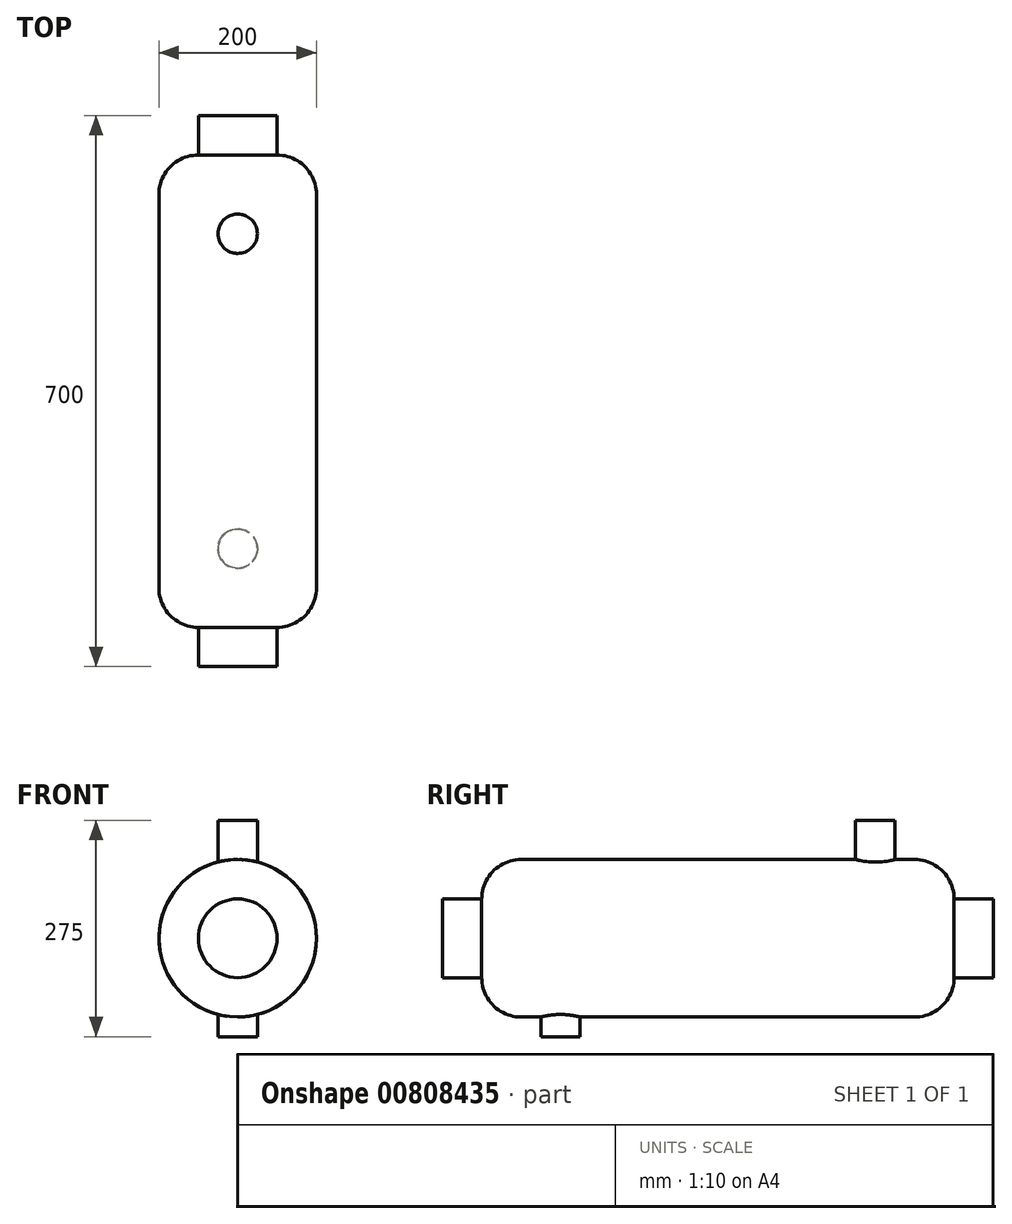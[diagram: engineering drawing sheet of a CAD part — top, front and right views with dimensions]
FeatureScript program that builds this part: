
annotation { "Feature Type Name" : "Feature", "Feature Type Description" : "" }
export const myFeature = defineFeature(function(context is Context, id is Id, definition is map)
    precondition{}
    {
        {
            var Q0;
            Q0=qCreatedBy(makeId("Right.planeOp"),FACE);
            var sketch = newSketch(context, id + "F0", { "sketchPlane" : qUnion([Q0])});
            skPoint(sketch, "E0.middle", {"position": v(0, 0) * mm});
            skLineSegment(sketch, "E1", {"start": v(0, 0) * mm, "end": v(-300, 0) * mm});
            skLineSegment(sketch, "E2", {"start": v(-300, 0) * mm, "end": v(-300, 50) * mm});
            skLineSegment(sketch, "E3", {"start": v(-250, 100) * mm, "end": v(250, 100) * mm});
            skLineSegment(sketch, "E4", {"start": v(300, 50) * mm, "end": v(300, 0) * mm});
            skLineSegment(sketch, "E5", {"start": v(300, 0) * mm, "end": v(0, 0) * mm});
            skPoint(sketch, "E6.visualSharp", {"position": v(-300, 100) * mm});
            skArc(sketch, "E6.filletArc", {"start": v(-250, 100) * mm, "mid": v(-285.36, 85.36) * mm, "end": v(-300, 50) * mm});
            skPoint(sketch, "E7.visualSharp", {"position": v(300, 100) * mm});
            skArc(sketch, "E7.filletArc", {"start": v(300, 50) * mm, "mid": v(285.36, 85.36) * mm, "end": v(250, 100) * mm});
            skLineSegment(sketch, "E8.bottom", {"start": v(-300, 0) * mm, "end": v(-300, 0) * mm});
            skLineSegment(sketch, "E8.top", {"start": v(-300, 50) * mm, "end": v(-300, 50) * mm});
            skLineSegment(sketch, "E9.bottom", {"start": v(-300, 0) * mm, "end": v(-350, 0) * mm});
            skLineSegment(sketch, "E9.top", {"start": v(-300, 50) * mm, "end": v(-350, 50) * mm});
            skLineSegment(sketch, "E9.right", {"start": v(-350, 0) * mm, "end": v(-350, 50) * mm});
            skLineSegment(sketch, "E10.bottom", {"start": v(300, 0) * mm, "end": v(350, 0) * mm});
            skLineSegment(sketch, "E10.top", {"start": v(300, 50) * mm, "end": v(350, 50) * mm});
            skLineSegment(sketch, "E10.left", {"start": v(300, 0) * mm, "end": v(300, 50) * mm});
            skLineSegment(sketch, "E10.right", {"start": v(350, 0) * mm, "end": v(350, 50) * mm});
            skLineSegment(sketch, "E11", {"start": v(-378.43, 0) * mm, "end": v(537.44, 0) * mm, "construction": true});
            skSolve(sketch);
        }
        {
            var Q0;
            Q0=makeQuery(id+"F0.imprint","IMPRINT",FACE,{"disambiguationData":[TD([[makeQuery(id+"F0.imprint","IMPRINT",EDGE,{"derivedFrom":sQuery(id+"F0.wireOp",EDGE,"E9.bottom")}),-1.0]])]});
            var Q1;
            Q1=makeQuery(id+"F0.imprint","IMPRINT",FACE,{"disambiguationData":[TD([[makeQuery(id+"F0.imprint","IMPRINT",EDGE,{"derivedFrom":sQuery(id+"F0.wireOp",EDGE,"E1")}),-1.0]])]});
            var Q2;
            Q2=makeQuery(id+"F0.imprint","IMPRINT",FACE,{"disambiguationData":[TD([[makeQuery(id+"F0.imprint","IMPRINT",EDGE,{"derivedFrom":sQuery(id+"F0.wireOp",EDGE,"E10.bottom")}),1.0]])]});
            var Q3;
            Q3=sQuery(id+"F0.wireOp",EDGE,"E11");
            revolve(context, id + "F1", {"surfaceOperationType" : NewSurfaceOperationType.NEW, "entities" : qUnion([Q0, Q1, Q2]), "axis" : qUnion([Q3]), "revolveType" : RevolveType.FULL});
        }
        {
            var Q0;
            Q0=qCreatedBy(makeId("Top.planeOp"),FACE);
            var sketch = newSketch(context, id + "F2", { "sketchPlane" : qUnion([Q0])});
            skCircle(sketch, "E12", {"center": v(0, 200) * mm, "radius": 25 * mm});
            skCircle(sketch, "E13", {"center": v(0, -200) * mm, "radius": 25 * mm});
            skSolve(sketch);
        }
        {
            var Q0;
            Q0=makeQuery(id+"F2.imprint","IMPRINT",FACE,{"disambiguationData":[TD([[makeQuery(id+"F2.imprint","IMPRINT",EDGE,{"derivedFrom":sQuery(id+"F2.wireOp",EDGE,"E12")}),1.0]])]});
            var Q1;
            Q1=sQuery(id+"F2.wireOp",EDGE,"E12");
            extrude(context, id + "F3", {"entities" : qUnion([Q0]), "operationType" : NewBodyOperationType.ADD, "surfaceOperationType" : NewSurfaceOperationType.ADD, "surfaceEntities" : qUnion([Q1]), "depth" : 150 * mm, "offsetDistance" : 25 * mm});
        }
        {
            var Q0;
            Q0=makeQuery(id+"F2.imprint","IMPRINT",FACE,{"disambiguationData":[TD([[makeQuery(id+"F2.imprint","IMPRINT",EDGE,{"derivedFrom":sQuery(id+"F2.wireOp",EDGE,"E13")}),1.0]])]});
            extrude(context, id + "F4", {"entities" : qUnion([Q0]), "operationType" : NewBodyOperationType.ADD, "oppositeDirection" : true, "depth" : 125 * mm, "offsetDistance" : 25 * mm});
        }
    });
